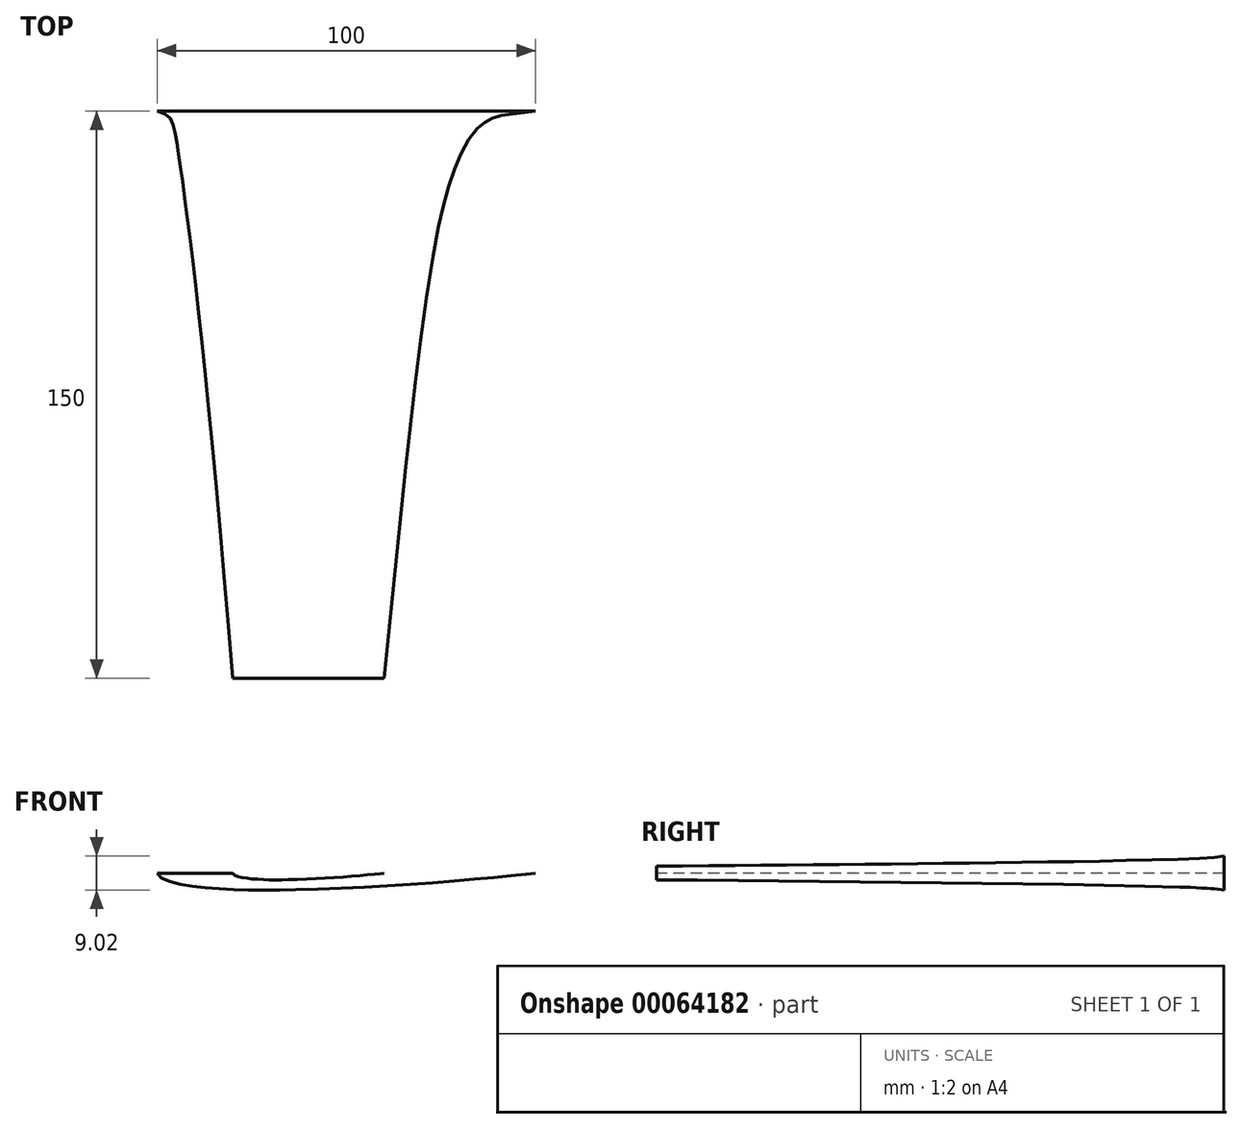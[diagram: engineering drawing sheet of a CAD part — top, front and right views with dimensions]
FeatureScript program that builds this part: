
annotation { "Feature Type Name" : "Feature", "Feature Type Description" : "" }
export const myFeature = defineFeature(function(context is Context, id is Id, definition is map)
    precondition{}
    {
        {
            var Q0;
            Q0=qCreatedBy(makeId("Front.planeOp"),FACE);
            var sketch = newSketch(context, id + "F0", { "sketchPlane" : qUnion([Q0])});
            skLineSegment(sketch, "E0", {"start": v(-50, 0) * mm, "end": v(50, 0) * mm, "construction": true});
            skPoint(sketch, "E1", {"position": v(-49.9, 0.35) * mm});
            skPoint(sketch, "E2", {"position": v(-49.57, 0.77) * mm});
            skPoint(sketch, "E3", {"position": v(-49.04, 1.21) * mm});
            skPoint(sketch, "E4", {"position": v(-48.3, 1.65) * mm});
            skPoint(sketch, "E5", {"position": v(-47.35, 2.04) * mm});
            skPoint(sketch, "E6", {"position": v(-46.2, 2.4) * mm});
            skPoint(sketch, "E7", {"position": v(-44.84, 2.72) * mm});
            skPoint(sketch, "E8", {"position": v(-43.3, 3.02) * mm});
            skPoint(sketch, "E9", {"position": v(-41.57, 3.3) * mm});
            skPoint(sketch, "E10", {"position": v(-39.67, 3.56) * mm});
            skPoint(sketch, "E11", {"position": v(-37.6, 3.8) * mm});
            skPoint(sketch, "E12", {"position": v(-35.36, 4) * mm});
            skPoint(sketch, "E13", {"position": v(-32.97, 4.16) * mm});
            skPoint(sketch, "E14", {"position": v(-30.44, 4.3) * mm});
            skPoint(sketch, "E15", {"position": v(-27.78, 4.4) * mm});
            skPoint(sketch, "E16", {"position": v(-25, 4.47) * mm});
            skPoint(sketch, "E17", {"position": v(-22.11, 4.5) * mm});
            skPoint(sketch, "E18", {"position": v(-19.13, 4.5) * mm});
            skPoint(sketch, "E19", {"position": v(-16.07, 4.48) * mm});
            skPoint(sketch, "E20", {"position": v(-12.94, 4.43) * mm});
            skPoint(sketch, "E21", {"position": v(-6.53, 4.25) * mm});
            skPoint(sketch, "E22", {"position": v(0, 3.98) * mm});
            skPoint(sketch, "E23", {"position": v(6.53, 3.64) * mm});
            skPoint(sketch, "E24", {"position": v(12.94, 3.25) * mm});
            skPoint(sketch, "E25", {"position": v(19.13, 2.82) * mm});
            skPoint(sketch, "E26", {"position": v(25, 2.38) * mm});
            skPoint(sketch, "E27", {"position": v(30.44, 1.95) * mm});
            skPoint(sketch, "E28", {"position": v(35.35, 1.52) * mm});
            skPoint(sketch, "E29", {"position": v(39.67, 1.13) * mm});
            skPoint(sketch, "E30", {"position": v(43.3, 0.77) * mm});
            skPoint(sketch, "E31", {"position": v(46.2, 0.46) * mm});
            skPoint(sketch, "E32", {"position": v(48.3, 0.22) * mm});
            skPoint(sketch, "E33", {"position": v(-49.9, -0.35) * mm});
            skPoint(sketch, "E34", {"position": v(-49.57, -0.77) * mm});
            skPoint(sketch, "E35", {"position": v(-49.04, -1.21) * mm});
            skPoint(sketch, "E36", {"position": v(-48.3, -1.65) * mm});
            skPoint(sketch, "E37", {"position": v(-47.35, -2.04) * mm});
            skPoint(sketch, "E38", {"position": v(-46.2, -2.4) * mm});
            skPoint(sketch, "E39", {"position": v(-44.84, -2.72) * mm});
            skPoint(sketch, "E40", {"position": v(-43.3, -3.02) * mm});
            skPoint(sketch, "E41", {"position": v(-41.57, -3.3) * mm});
            skPoint(sketch, "E42", {"position": v(-39.67, -3.56) * mm});
            skPoint(sketch, "E43", {"position": v(-37.6, -3.8) * mm});
            skPoint(sketch, "E44", {"position": v(-35.36, -4) * mm});
            skPoint(sketch, "E45", {"position": v(-32.97, -4.16) * mm});
            skPoint(sketch, "E46", {"position": v(-30.44, -4.3) * mm});
            skPoint(sketch, "E47", {"position": v(-27.78, -4.4) * mm});
            skPoint(sketch, "E48", {"position": v(-25, -4.47) * mm});
            skPoint(sketch, "E49", {"position": v(-22.11, -4.5) * mm});
            skPoint(sketch, "E50", {"position": v(-19.13, -4.5) * mm});
            skPoint(sketch, "E51", {"position": v(-16.07, -4.48) * mm});
            skPoint(sketch, "E52", {"position": v(-12.94, -4.43) * mm});
            skPoint(sketch, "E53", {"position": v(-6.53, -4.25) * mm});
            skPoint(sketch, "E54", {"position": v(0, -3.98) * mm});
            skPoint(sketch, "E55", {"position": v(6.53, -3.64) * mm});
            skPoint(sketch, "E56", {"position": v(12.94, -3.25) * mm});
            skPoint(sketch, "E57", {"position": v(19.13, -2.82) * mm});
            skPoint(sketch, "E58", {"position": v(25, -2.38) * mm});
            skPoint(sketch, "E59", {"position": v(30.44, -1.94) * mm});
            skPoint(sketch, "E60", {"position": v(35.35, -1.52) * mm});
            skPoint(sketch, "E61", {"position": v(39.67, -1.13) * mm});
            skPoint(sketch, "E62", {"position": v(43.3, -0.77) * mm});
            skPoint(sketch, "E63", {"position": v(46.2, -0.46) * mm});
            skPoint(sketch, "E64", {"position": v(48.3, -0.22) * mm});
            skPoint(sketch, "E65", {"position": v(49.57, 0.06) * mm});
            skPoint(sketch, "E66", {"position": v(49.57, -0.06) * mm});
            skFitSpline(sketch, "E67", {"points": [v(50, 0) * mm, v(49.57, 0.06) * mm, v(48.3, 0.22) * mm, v(46.2, 0.46) * mm, v(43.3, 0.77) * mm, v(39.67, 1.13) * mm, v(35.35, 1.52) * mm, v(30.44, 1.95) * mm, v(25, 2.38) * mm, v(19.13, 2.82) * mm, v(12.94, 3.25) * mm, v(6.53, 3.64) * mm, v(0, 3.98) * mm, v(-6.53, 4.25) * mm, v(-12.94, 4.43) * mm, v(-16.07, 4.48) * mm, v(-19.13, 4.5) * mm, v(-22.11, 4.5) * mm, v(-25, 4.47) * mm, v(-27.78, 4.4) * mm, v(-30.44, 4.3) * mm, v(-32.97, 4.16) * mm, v(-35.36, 4) * mm, v(-37.6, 3.8) * mm, v(-39.67, 3.56) * mm, v(-41.57, 3.3) * mm, v(-43.3, 3.02) * mm, v(-44.84, 2.72) * mm, v(-46.2, 2.4) * mm, v(-47.35, 2.04) * mm, v(-48.3, 1.65) * mm, v(-49.04, 1.21) * mm, v(-49.57, 0.77) * mm, v(-49.9, 0.35) * mm, v(-50, 0) * mm, v(-49.9, -0.35) * mm, v(-49.57, -0.77) * mm, v(-49.04, -1.21) * mm, v(-48.3, -1.65) * mm, v(-47.35, -2.04) * mm, v(-46.2, -2.4) * mm, v(-44.84, -2.72) * mm, v(-43.3, -3.02) * mm, v(-41.57, -3.3) * mm, v(-39.67, -3.56) * mm, v(-37.6, -3.8) * mm, v(-35.36, -4) * mm, v(-32.97, -4.16) * mm, v(-30.44, -4.3) * mm, v(-27.78, -4.4) * mm, v(-25, -4.47) * mm, v(-22.11, -4.5) * mm, v(-19.13, -4.5) * mm, v(-16.07, -4.48) * mm, v(-12.94, -4.43) * mm, v(-6.53, -4.25) * mm, v(0, -3.98) * mm, v(6.53, -3.64) * mm, v(12.94, -3.25) * mm, v(19.13, -2.82) * mm, v(25, -2.38) * mm, v(30.44, -1.94) * mm, v(35.35, -1.52) * mm, v(39.67, -1.13) * mm, v(43.3, -0.77) * mm, v(46.2, -0.46) * mm, v(48.3, -0.22) * mm, v(49.57, -0.06) * mm, v(50, 0) * mm]});
            skSolve(sketch);
        }
        {
            var Q0;
            Q0=qCreatedBy(makeId("Top.planeOp"),FACE);
            var sketch = newSketch(context, id + "F1", { "sketchPlane" : qUnion([Q0])});
            skLineSegment(sketch, "E68", {"start": v(-30, -150) * mm, "end": v(10, -150) * mm});
            skLineSegment(sketch, "E69", {"start": v(-50, 0) * mm, "end": v(50, 0) * mm});
            skFitSpline(sketch, "E70", {"points": [v(-30, -150) * mm, v(-45, -7.15) * mm, v(-50, 0) * mm], "startDerivative": vector(-26.82, 327.76) * mm, "endDerivative": vector(-59.45, 11.44) * mm});
            skFitSpline(sketch, "E71", {"points": [v(10, -150) * mm, v(35.86, -3.52) * mm, v(50, 0) * mm], "startDerivative": vector(34.31, 327.44) * mm, "endDerivative": vector(58.17, 13.04) * mm});
            skSolve(sketch);
        }
        {
            var Q0;
            Q0=qCreatedBy(makeId("Front.planeOp"),FACE);
            cPlane(context, id + "F2", {"entities" : qUnion([Q0]), "cplaneType" : CPlaneType.OFFSET, "offset" : 150 * mm, "width" : 150 * mm, "height" : 150 * mm});
        }
        {
            var Q0;
            Q0=qCreatedBy(id+"F2.planeOp",FACE);
            var sketch = newSketch(context, id + "F3", { "sketchPlane" : qUnion([Q0])});
            skLineSegment(sketch, "E72", {"start": v(-30, 0) * mm, "end": v(10, 0) * mm, "construction": true});
            skPoint(sketch, "E73", {"position": v(-29.96, 0.14) * mm});
            skPoint(sketch, "E74", {"position": v(-29.83, 0.3) * mm});
            skPoint(sketch, "E75", {"position": v(-29.62, 0.49) * mm});
            skPoint(sketch, "E76", {"position": v(-29.32, 0.66) * mm});
            skPoint(sketch, "E77", {"position": v(-28.94, 0.82) * mm});
            skPoint(sketch, "E78", {"position": v(-28.48, 0.96) * mm});
            skPoint(sketch, "E79", {"position": v(-27.94, 1.09) * mm});
            skPoint(sketch, "E80", {"position": v(-27.32, 1.2) * mm});
            skPoint(sketch, "E81", {"position": v(-26.63, 1.32) * mm});
            skPoint(sketch, "E82", {"position": v(-25.87, 1.43) * mm});
            skPoint(sketch, "E83", {"position": v(-25.04, 1.52) * mm});
            skPoint(sketch, "E84", {"position": v(-24.14, 1.6) * mm});
            skPoint(sketch, "E85", {"position": v(-23.19, 1.66) * mm});
            skPoint(sketch, "E86", {"position": v(-22.18, 1.72) * mm});
            skPoint(sketch, "E87", {"position": v(-21.11, 1.76) * mm});
            skPoint(sketch, "E88", {"position": v(-20, 1.79) * mm});
            skPoint(sketch, "E89", {"position": v(-18.85, 1.8) * mm});
            skPoint(sketch, "E90", {"position": v(-17.65, 1.8) * mm});
            skPoint(sketch, "E91", {"position": v(-16.43, 1.8) * mm});
            skPoint(sketch, "E92", {"position": v(-15.18, 1.77) * mm});
            skPoint(sketch, "E93", {"position": v(-12.61, 1.7) * mm});
            skPoint(sketch, "E94", {"position": v(-10, 1.6) * mm});
            skPoint(sketch, "E95", {"position": v(-7.39, 1.46) * mm});
            skPoint(sketch, "E96", {"position": v(-4.82, 1.3) * mm});
            skPoint(sketch, "E97", {"position": v(-2.35, 1.13) * mm});
            skPoint(sketch, "E98", {"position": v(0, 0.95) * mm});
            skPoint(sketch, "E99", {"position": v(2.18, 0.78) * mm});
            skPoint(sketch, "E100", {"position": v(4.14, 0.6) * mm});
            skPoint(sketch, "E101", {"position": v(5.87, 0.45) * mm});
            skPoint(sketch, "E102", {"position": v(7.32, 0.3) * mm});
            skPoint(sketch, "E103", {"position": v(8.48, 0.19) * mm});
            skPoint(sketch, "E104", {"position": v(9.32, 0.09) * mm});
            skPoint(sketch, "E105", {"position": v(-29.96, -0.14) * mm});
            skPoint(sketch, "E106", {"position": v(-29.83, -0.3) * mm});
            skPoint(sketch, "E107", {"position": v(-29.62, -0.49) * mm});
            skPoint(sketch, "E108", {"position": v(-29.32, -0.66) * mm});
            skPoint(sketch, "E109", {"position": v(-28.94, -0.82) * mm});
            skPoint(sketch, "E110", {"position": v(-28.48, -0.96) * mm});
            skPoint(sketch, "E111", {"position": v(-27.94, -1.09) * mm});
            skPoint(sketch, "E112", {"position": v(-27.32, -1.2) * mm});
            skPoint(sketch, "E113", {"position": v(-26.63, -1.32) * mm});
            skPoint(sketch, "E114", {"position": v(-25.87, -1.43) * mm});
            skPoint(sketch, "E115", {"position": v(-25.04, -1.52) * mm});
            skPoint(sketch, "E116", {"position": v(-24.14, -1.6) * mm});
            skPoint(sketch, "E117", {"position": v(-23.19, -1.66) * mm});
            skPoint(sketch, "E118", {"position": v(-22.18, -1.72) * mm});
            skPoint(sketch, "E119", {"position": v(-21.11, -1.76) * mm});
            skPoint(sketch, "E120", {"position": v(-20, -1.79) * mm});
            skPoint(sketch, "E121", {"position": v(-18.85, -1.8) * mm});
            skPoint(sketch, "E122", {"position": v(-17.65, -1.8) * mm});
            skPoint(sketch, "E123", {"position": v(-16.43, -1.8) * mm});
            skPoint(sketch, "E124", {"position": v(-15.18, -1.77) * mm});
            skPoint(sketch, "E125", {"position": v(-12.61, -1.7) * mm});
            skPoint(sketch, "E126", {"position": v(-10, -1.6) * mm});
            skPoint(sketch, "E127", {"position": v(-7.39, -1.46) * mm});
            skPoint(sketch, "E128", {"position": v(-4.82, -1.3) * mm});
            skPoint(sketch, "E129", {"position": v(-2.35, -1.13) * mm});
            skPoint(sketch, "E130", {"position": v(0, -0.95) * mm});
            skPoint(sketch, "E131", {"position": v(2.18, -0.78) * mm});
            skPoint(sketch, "E132", {"position": v(4.14, -0.6) * mm});
            skPoint(sketch, "E133", {"position": v(5.87, -0.45) * mm});
            skPoint(sketch, "E134", {"position": v(7.32, -0.3) * mm});
            skPoint(sketch, "E135", {"position": v(8.48, -0.19) * mm});
            skPoint(sketch, "E136", {"position": v(9.32, -0.09) * mm});
            skPoint(sketch, "E137", {"position": v(9.83, 0.02) * mm});
            skPoint(sketch, "E138", {"position": v(9.83, -0.02) * mm});
            skFitSpline(sketch, "E139", {"points": [v(10, 0) * mm, v(9.83, 0.02) * mm, v(9.32, 0.09) * mm, v(8.48, 0.19) * mm, v(7.32, 0.3) * mm, v(5.87, 0.45) * mm, v(4.14, 0.6) * mm, v(2.18, 0.78) * mm, v(0, 0.95) * mm, v(-2.35, 1.13) * mm, v(-4.82, 1.3) * mm, v(-7.39, 1.46) * mm, v(-10, 1.6) * mm, v(-12.61, 1.7) * mm, v(-15.18, 1.77) * mm, v(-16.43, 1.8) * mm, v(-17.65, 1.8) * mm, v(-18.85, 1.8) * mm, v(-20, 1.79) * mm, v(-21.11, 1.76) * mm, v(-22.18, 1.72) * mm, v(-23.19, 1.66) * mm, v(-24.14, 1.6) * mm, v(-25.04, 1.52) * mm, v(-25.87, 1.43) * mm, v(-26.63, 1.32) * mm, v(-27.32, 1.2) * mm, v(-27.94, 1.09) * mm, v(-28.48, 0.96) * mm, v(-28.94, 0.82) * mm, v(-29.32, 0.66) * mm, v(-29.62, 0.49) * mm, v(-29.83, 0.3) * mm, v(-29.96, 0.14) * mm, v(-30, 0) * mm, v(-29.96, -0.14) * mm, v(-29.83, -0.3) * mm, v(-29.62, -0.49) * mm, v(-29.32, -0.66) * mm, v(-28.94, -0.82) * mm, v(-28.48, -0.96) * mm, v(-27.94, -1.09) * mm, v(-27.32, -1.2) * mm, v(-26.63, -1.32) * mm, v(-25.87, -1.43) * mm, v(-25.04, -1.52) * mm, v(-24.14, -1.6) * mm, v(-23.19, -1.66) * mm, v(-22.18, -1.72) * mm, v(-21.11, -1.76) * mm, v(-20, -1.79) * mm, v(-18.85, -1.8) * mm, v(-17.65, -1.8) * mm, v(-16.43, -1.8) * mm, v(-15.18, -1.77) * mm, v(-12.61, -1.7) * mm, v(-10, -1.6) * mm, v(-7.39, -1.46) * mm, v(-4.82, -1.3) * mm, v(-2.35, -1.13) * mm, v(0, -0.95) * mm, v(2.18, -0.78) * mm, v(4.14, -0.6) * mm, v(5.87, -0.45) * mm, v(7.32, -0.3) * mm, v(8.48, -0.19) * mm, v(9.32, -0.09) * mm, v(9.83, -0.02) * mm, v(10, 0) * mm]});
            skSolve(sketch);
        }
        {
            var Q0;
            Q0=makeQuery(id+"F0.imprint","IMPRINT",FACE,{"disambiguationData":[TD([[makeQuery(id+"F0.imprint","IMPRINT",EDGE,{"derivedFrom":sQuery(id+"F0.wireOp",EDGE,"E67")}),1.0]])]});
            var Q1;
            Q1=makeQuery(id+"F3.imprint","IMPRINT",FACE,{"disambiguationData":[TD([[makeQuery(id+"F3.imprint","IMPRINT",EDGE,{"derivedFrom":sQuery(id+"F3.wireOp",EDGE,"E139")}),1.0]])]});
            var Q2;
            Q2=sQuery(id+"F1.wireOp",EDGE,"E70");
            var Q3;
            Q3=sQuery(id+"F1.wireOp",EDGE,"E71");
            loft(context, id + "F4", {"addGuides" : true, "sheetProfilesArray" : [{ "sheetProfileEntities" : qUnion([Q0]) }, { "sheetProfileEntities" : qUnion([Q1]) }], "guidesArray" : [{ "guideEntities" : qUnion([Q2]), "guideDerivativeType" : LoftGuideDerivativeType.DEFAULT, "guideDerivativeMagnitude" : 1 }, { "guideEntities" : qUnion([Q3]), "guideDerivativeType" : LoftGuideDerivativeType.DEFAULT, "guideDerivativeMagnitude" : 1 }]});
        }
    });
